# Revit family: 307_2c91688fe4b84a309d506ab36b2033
name_source: partatom
category: Pipe Accessories
units: mm (PartAtom-declared; Revit-internal decimal feet)

## family parameters
Always vertical = Yes
Cut with Voids When Loaded = No
Part Type = Breaks Into
Round Connector Dimension = Use Diameter
Shared = No
Work Plane-Based = No

## types (4) — shared parameters
B1 = 2 mm  [stored 0.00656168 ft]
B11 = 13 mm  [stored 0.0426509 ft]
B11__ve = -13 mm  [stored -0.0426509 ft]
B1__ve = -2 mm  [stored -0.00656168 ft]
CenSd_NR1_6 = 14 mm  [stored 0.0459318 ft]
CenSd_NR_6 = 10 mm  [stored 0.0328084 ft]
Description = Flanged hydraulic separator, air vent and drain valve
E1 = 7 mm  [stored 0.0229659 ft]
E2 = 13 mm  [stored 0.0426509 ft]
E3 = 26 mm
ER = 72 mm
HD2 = 5 mm  [stored 0.0164042 ft]
L2D = 511 mm
L2D_Min = 3048 mm
Manufacturer = FAR
NR = 11 mm
NR1 = 16 mm
QmdConnectorList = 301;D;302;D
R2 = 13 mm  [stored 0.0426509 ft]
RH = 12 mm  [stored 0.0393701 ft]
RR = 8 mm  [stored 0.0262467 ft]
W2D = 100 mm  [stored 0.328084 ft]
magiPartTypeId = 307
magiProductFamilyId = 2c91688fe4b84a309d506ab36b2033

## per-type parameters (varying)
| type | B | C | D | D12 | DM1 | DM2 | G | H | HC | HCD2 | HE | HE1 | HT | H__ve | L1 | LL | LM | R | RC | magiProductId |
| 2164 100 | 280 mm | 450 mm | 100 mm | 75 mm  [stored 0.246063 ft] | 60 mm  [stored 0.19685 ft] | 48 mm  [stored 0.15748 ft] | 167 mm  [stored 0.5479 ft] | 184 mm  [stored 0.603675 ft] | 42 mm | 60 mm  [stored 0.19685 ft] | Yes | No | 230 mm  [stored 0.754593 ft] | -184 mm  [stored -0.603675 ft] | 26 mm | 256 mm | 430 mm | 50 mm  [stored 0.164042 ft] | 46 mm  [stored 0.150919 ft] | 30c19fde536d4b7e80c20b45797d6a |
| 2164 50 | 234 mm | 330 mm | 50 mm | 50 mm  [stored 0.164042 ft] | 30 mm  [stored 0.0984252 ft] | 32 mm  [stored 0.104987 ft] | 114 mm | 132 mm | 28 mm | 40 mm  [stored 0.131234 ft] | No | Yes | 184 mm  [stored 0.603675 ft] | -132 mm | 20 mm  [stored 0.0656168 ft] | 197 mm | 324 mm | 25 mm  [stored 0.082021 ft] | 37 mm  [stored 0.121391 ft] | d7ccfda699b2448dad43ceb41c4096 |
| 2164 65 | 234 mm | 330 mm | 65 mm | 50 mm  [stored 0.164042 ft] | 39 mm  [stored 0.127953 ft] | 32 mm  [stored 0.104987 ft] | 114 mm | 132 mm | 28 mm | 40 mm  [stored 0.131234 ft] | Yes | No | 184 mm  [stored 0.603675 ft] | -132 mm | 20 mm  [stored 0.0656168 ft] | 197 mm | 324 mm | 33 mm | 37 mm  [stored 0.121391 ft] | 71a9aff40bd94d57948ff36d22586c |
| 2164 80 | 280 mm | 450 mm | 80 mm | 75 mm  [stored 0.246063 ft] | 48 mm  [stored 0.15748 ft] | 48 mm  [stored 0.15748 ft] | 167 mm  [stored 0.5479 ft] | 184 mm  [stored 0.603675 ft] | 42 mm | 60 mm  [stored 0.19685 ft] | Yes | No | 230 mm  [stored 0.754593 ft] | -184 mm  [stored -0.603675 ft] | 26 mm | 256 mm | 430 mm | 40 mm  [stored 0.131234 ft] | 46 mm  [stored 0.150919 ft] | f38ff9a0e22c45cabc91b409692365 |

note: column(s) folded — value = type name in every type: MC Product Code

note: [stored X ft] marks values corroborated as IEEE doubles in the binary element streams (Revit-internal decimal feet)

## geometry (parser evidence)
native form markers: Sweep x3
no freeform markers — native parametric forms only
